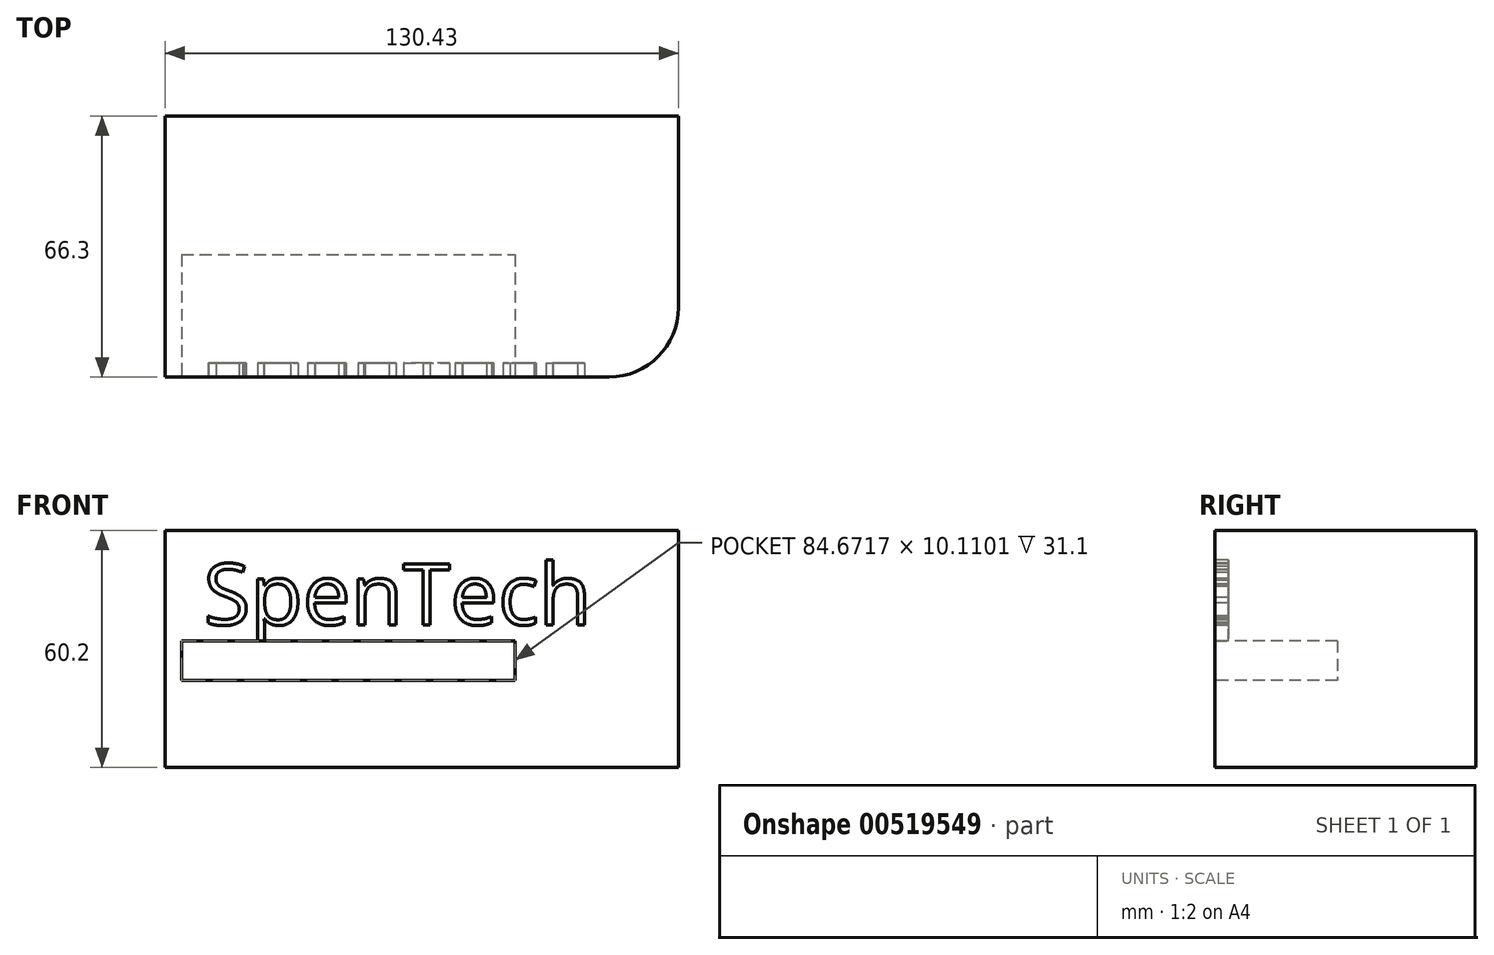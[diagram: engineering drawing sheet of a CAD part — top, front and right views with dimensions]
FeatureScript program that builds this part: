
annotation { "Feature Type Name" : "Feature", "Feature Type Description" : "" }
export const myFeature = defineFeature(function(context is Context, id is Id, definition is map)
    precondition{}
    {
        {
            var Q0;
            Q0=qCreatedBy(makeId("Front.planeOp"),FACE);
            var sketch = newSketch(context, id + "F0", { "sketchPlane" : qUnion([Q0])});
            skLineSegment(sketch, "E0.bottom", {"start": v(-72.06, 33.04) * mm, "end": v(58.37, 33.04) * mm});
            skLineSegment(sketch, "E0.top", {"start": v(-72.06, -27.16) * mm, "end": v(58.37, -27.16) * mm});
            skLineSegment(sketch, "E0.left", {"start": v(-72.06, 33.04) * mm, "end": v(-72.06, -27.16) * mm});
            skLineSegment(sketch, "E0.right", {"start": v(58.37, 33.04) * mm, "end": v(58.37, -27.16) * mm});
            skSolve(sketch);
        }
        {
            var Q0;
            Q0=makeQuery(id+"F0.imprint","IMPRINT",FACE,{"disambiguationData":[TD([[makeQuery(id+"F0.imprint","IMPRINT",EDGE,{"derivedFrom":sQuery(id+"F0.wireOp",EDGE,"E0.bottom")}),-1.0]])]});
            var sketch = newSketch(context, id + "F1", { "sketchPlane" : qUnion([Q0])});
            skSolve(sketch);
        }
        {
            var Q0;
            Q0 = qSketchRegion(id + "F1", true);
            var Q1;
            Q1=makeQuery(id+"F0.imprint","IMPRINT",FACE,{"disambiguationData":[TD([[makeQuery(id+"F0.imprint","IMPRINT",EDGE,{"derivedFrom":sQuery(id+"F0.wireOp",EDGE,"E0.bottom")}),-1.0]])]});
            extrude(context, id + "F2", {"entities" : qUnion([Q0, Q1]), "depth" : 66.3 * mm, "offsetDistance" : 25 * mm});
        }
        {
            var Q0;
            Q0=makeQuery(id+"F2.opExtrude","CAP_FACE",FACE,{"disambiguationData":[OSD([sQuery(id+"F0.wireOp",EDGE,"E0.bottom"),sQuery(id+"F0.wireOp",EDGE,"E0.top"),sQuery(id+"F0.wireOp",EDGE,"E0.left"),sQuery(id+"F0.wireOp",EDGE,"E0.right")])],"isStart":false});
            var sketch = newSketch(context, id + "F3", { "sketchPlane" : qUnion([Q0])});
            skLineSegment(sketch, "E1.bottom", {"start": v(-67.85, 5.03) * mm, "end": v(16.82, 5.03) * mm});
            skLineSegment(sketch, "E1.top", {"start": v(-67.85, -5.08) * mm, "end": v(16.82, -5.08) * mm});
            skLineSegment(sketch, "E1.left", {"start": v(-67.85, 5.03) * mm, "end": v(-67.85, -5.08) * mm});
            skLineSegment(sketch, "E1.right", {"start": v(16.82, 5.03) * mm, "end": v(16.82, -5.08) * mm});
            skSolve(sketch);
        }
        {
            var Q0;
            Q0=makeQuery(id+"F3.imprint","IMPRINT",FACE,{"disambiguationData":[TD([[makeQuery(id+"F3.imprint","IMPRINT",EDGE,{"derivedFrom":sQuery(id+"F3.wireOp",EDGE,"E1.bottom")}),-1.0]])]});
            var sketch = newSketch(context, id + "F4", { "sketchPlane" : qUnion([Q0])});
            skSolve(sketch);
        }
        {
            var Q0;
            Q0 = qSketchRegion(id + "F4", true);
            var Q1;
            Q1=makeQuery(id+"F3.imprint","IMPRINT",FACE,{"disambiguationData":[TD([[makeQuery(id+"F3.imprint","IMPRINT",EDGE,{"derivedFrom":sQuery(id+"F3.wireOp",EDGE,"E1.bottom")}),-1.0]])]});
            extrude(context, id + "F5", {"entities" : qUnion([Q0, Q1]), "operationType" : NewBodyOperationType.REMOVE, "oppositeDirection" : true, "depth" : 31.1 * mm, "offsetDistance" : 25 * mm});
        }
        {
            var Q0;
            Q0=makeQuery(id+"F2.opExtrude","CAP_FACE",FACE,{"disambiguationData":[OSD([sQuery(id+"F0.wireOp",EDGE,"E0.bottom"),sQuery(id+"F0.wireOp",EDGE,"E0.top"),sQuery(id+"F0.wireOp",EDGE,"E0.left"),sQuery(id+"F0.wireOp",EDGE,"E0.right")])],"isStart":false});
            var sketch = newSketch(context, id + "F6", { "sketchPlane" : qUnion([Q0])});
            skText(sketch, "E2", { "text": "SpenTech", "fontName": "OpenSans-Regular.ttf"});
            const initialGuessF6  = {"E2": [-0.06232, 0.00909, 1, 0, 0.01562]};
            skSetInitialGuess(sketch, initialGuessF6);
            skSolve(sketch);
        }
        {
            var Q0;
            Q0 = qSketchRegion(id + "F6", true);
            extrude(context, id + "F7", {"entities" : qUnion([Q0]), "operationType" : NewBodyOperationType.REMOVE, "oppositeDirection" : true, "depth" : 3.5 * mm, "offsetDistance" : 25 * mm});
        }
        {
            var Q0;
            Q0=makeQuery(id+"F2.opExtrude","CAP_EDGE",EDGE,{"disambiguationData":[OSD([sQuery(id+"F0.wireOp",EDGE,"E0.right")])],"isStart":false});
            fillet(context, id + "F8", {"entities" : qUnion([Q0]), "radius" : 17.62 * mm, "tangentPropagation" : true, "allowEdgeOverflow" : false});
        }
    });
